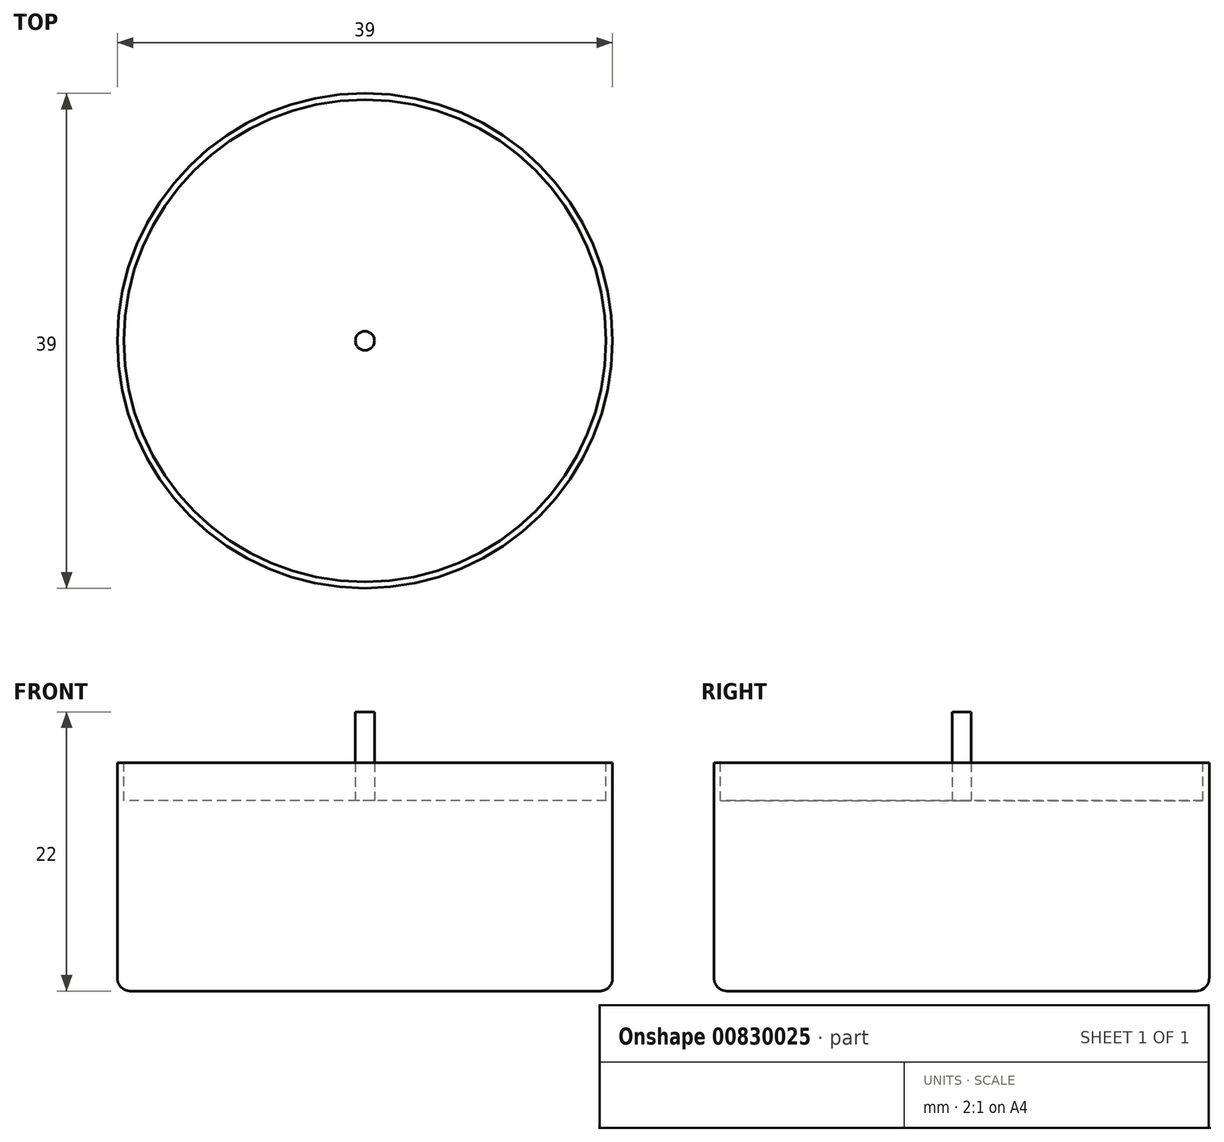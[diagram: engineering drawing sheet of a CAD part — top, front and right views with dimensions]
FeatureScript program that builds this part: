
annotation { "Feature Type Name" : "Feature", "Feature Type Description" : "" }
export const myFeature = defineFeature(function(context is Context, id is Id, definition is map)
    precondition{}
    {
        {
            var Q0;
            Q0=qCreatedBy(makeId("Top.planeOp"),FACE);
            var sketch = newSketch(context, id + "F0", { "sketchPlane" : qUnion([Q0])});
            skCircle(sketch, "E0", {"center": v(0, 0) * mm, "radius": 19.5 * mm});
            skSolve(sketch);
        }
        {
            var Q0;
            Q0=makeQuery(id+"F0.imprint","IMPRINT",FACE,{"disambiguationData":[TD([[makeQuery(id+"F0.imprint","IMPRINT",EDGE,{"derivedFrom":sQuery(id+"F0.wireOp",EDGE,"E0")}),1.0]])]});
            extrude(context, id + "F1", {"entities" : qUnion([Q0]), "depth" : 18 * mm, "offsetDistance" : 25 * mm});
        }
        {
            var Q0;
            Q0=makeQuery(id+"F1.opExtrude","CAP_FACE",FACE,{"disambiguationData":[OSD([sQuery(id+"F0.wireOp",EDGE,"E0")])],"isStart":false});
            var sketch = newSketch(context, id + "F2", { "sketchPlane" : qUnion([Q0])});
            skCircle(sketch, "E1", {"center": v(0, 0) * mm, "radius": 19 * mm});
            skSolve(sketch);
        }
        {
            var Q0;
            Q0=makeQuery(id+"F2.imprint","IMPRINT",FACE,{"disambiguationData":[TD([[makeQuery(id+"F2.imprint","IMPRINT",EDGE,{"derivedFrom":sQuery(id+"F2.wireOp",EDGE,"E1")}),1.0]])]});
            extrude(context, id + "F3", {"entities" : qUnion([Q0]), "operationType" : NewBodyOperationType.REMOVE, "oppositeDirection" : true, "depth" : 3 * mm, "offsetDistance" : 25 * mm});
        }
        {
            var Q0;
            Q0=makeQuery(id+"F3.boolean.opBoolean","COPY",FACE,{"derivedFrom":makeQuery(id+"F3.opExtrude","CAP_FACE",FACE,{"disambiguationData":[OSD([sQuery(id+"F2.wireOp",EDGE,"E1")])],"isStart":false})});
            var sketch = newSketch(context, id + "F4", { "sketchPlane" : qUnion([Q0])});
            skCircle(sketch, "E2", {"center": v(0, 0) * mm, "radius": 0.75 * mm});
            skSolve(sketch);
        }
        {
            var Q0;
            Q0=makeQuery(id+"F4.imprint","IMPRINT",FACE,{"disambiguationData":[TD([[makeQuery(id+"F4.imprint","IMPRINT",EDGE,{"derivedFrom":sQuery(id+"F4.wireOp",EDGE,"E2")}),1.0]])]});
            extrude(context, id + "F5", {"entities" : qUnion([Q0]), "operationType" : NewBodyOperationType.ADD, "depth" : 7 * mm, "offsetDistance" : 25 * mm});
        }
        {
            var Q0;
            Q0=makeQuery(id+"F1.opExtrude","CAP_EDGE",EDGE,{"disambiguationData":[OSD([sQuery(id+"F0.wireOp",EDGE,"E0")])],"isStart":true});
            fillet(context, id + "F6", {"entities" : qUnion([Q0]), "radius" : 1 * mm, "tangentPropagation" : true, "allowEdgeOverflow" : false});
        }
    });
